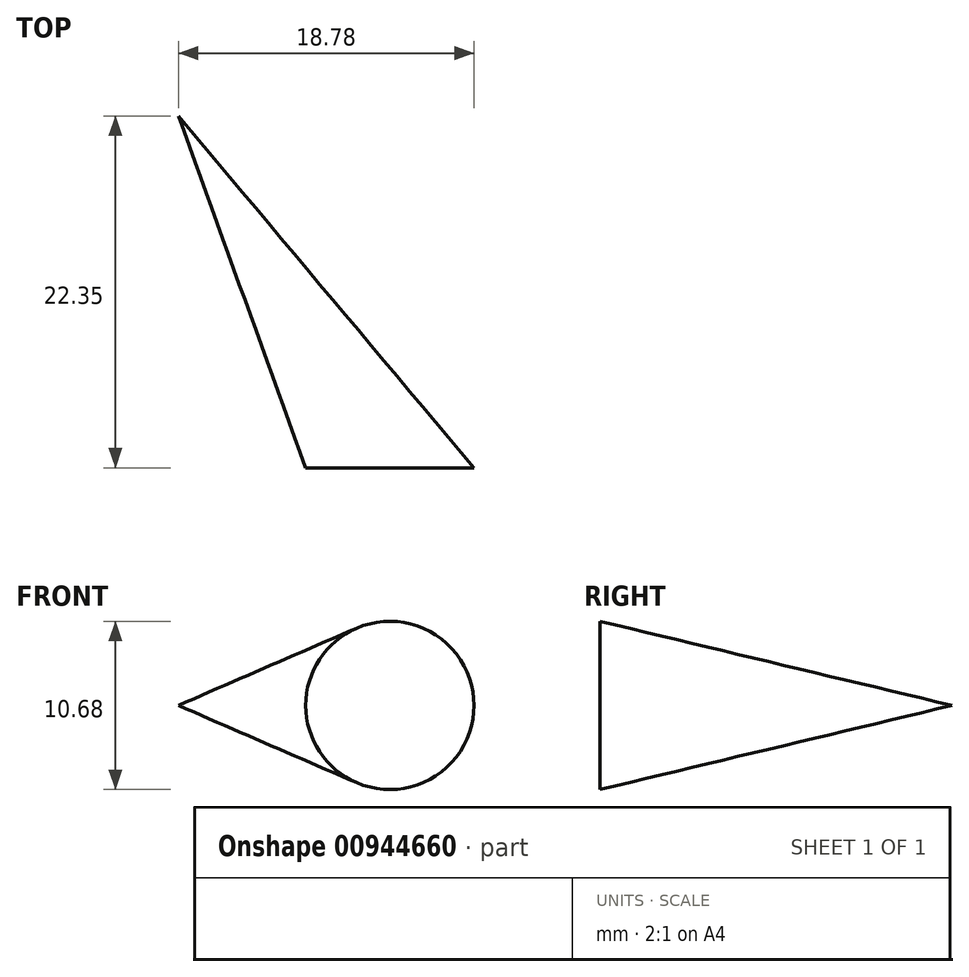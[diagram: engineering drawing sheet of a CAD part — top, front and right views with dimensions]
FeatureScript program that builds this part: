
annotation { "Feature Type Name" : "Feature", "Feature Type Description" : "" }
export const myFeature = defineFeature(function(context is Context, id is Id, definition is map)
    precondition{}
    {
        {
            var Q0;
            Q0=qCreatedBy(makeId("Front.planeOp"),FACE);
            cPlane(context, id + "F0", {"entities" : qUnion([Q0]), "cplaneType" : CPlaneType.OFFSET, "offset" : 47.75 * mm, "width" : 152.4 * mm, "height" : 152.4 * mm});
        }
        {
            var Q0;
            Q0=qCreatedBy(id+"F0.planeOp",FACE);
            var sketch = newSketch(context, id + "F1", { "sketchPlane" : qUnion([Q0])});
            skCircle(sketch, "E0", {"center": v(13.44, 0) * mm, "radius": 5.34 * mm});
            skSolve(sketch);
        }
        {
            var Q0;
            Q0=qCreatedBy(makeId("Front.planeOp"),FACE);
            cPlane(context, id + "F2", {"entities" : qUnion([Q0]), "cplaneType" : CPlaneType.OFFSET, "offset" : 25.4 * mm, "width" : 152.4 * mm, "height" : 152.4 * mm});
        }
        {
            var Q0;
            Q0=qCreatedBy(id+"F2.planeOp",FACE);
            var sketch = newSketch(context, id + "F3", { "sketchPlane" : qUnion([Q0])});
            skCircle(sketch, "E1", {"center": v(0, 0) * mm, "radius": 2.91 * mm});
            skSolve(sketch);
        }
        {
            var Q0;
            Q0=makeQuery(id+"F1.imprint","IMPRINT",FACE,{"disambiguationData":[TD([[makeQuery(id+"F1.imprint","IMPRINT",EDGE,{"derivedFrom":sQuery(id+"F1.wireOp",EDGE,"E0")}),1.0]])]});
            var Q1;
            Q1=sQuery(id+"F3.wireOp",VERTEX,"E1.center");
            loft(context, id + "F4", {"sheetProfilesArray" : [{ "sheetProfileEntities" : qUnion([Q0]) }, { "sheetProfileEntities" : qUnion([Q1]) }]});
        }
    });
